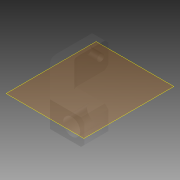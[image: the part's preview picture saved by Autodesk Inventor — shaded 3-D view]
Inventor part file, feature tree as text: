
AUTODESK INVENTOR PART (.ipt)
format: ipt  version: 2015 (Build 190159000, 159)  size: 126,464 bytes
history: native  units: mm
features: extrude x3, fillet x1, chamfer x1
ambient origin geometry x8: Origin, YZ Plane, XZ Plane, XY Plane, X Axis, Y Axis, Z Axis, Center Point
bodies: Solid1 (feature_tree)
feature tree (5):
  extrude  "Extrusión1"  Depth=14.0mm
  extrude  "Extrusión2"  Depth=4.0mm
  fillet  "Empalme1"  Radius=25.0mm
  extrude  "Extrusión4"  Depth=7.5mm
  chamfer  "Chaflán1"  Distance=48.0mm
